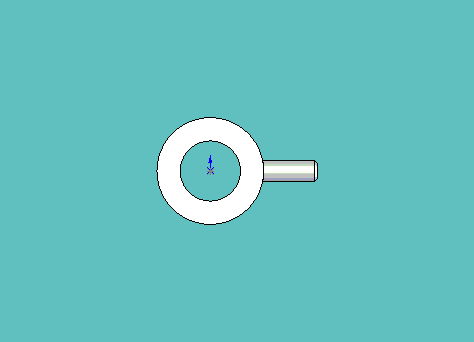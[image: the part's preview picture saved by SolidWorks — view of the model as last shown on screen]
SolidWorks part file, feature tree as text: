
SOLIDWORKS PART (.sldprt)
format: sldprt  version: not decoded by parser v0  size: 206,336 bytes
history: native  units: mm
features: sketch x2, material x1, extrude x1, revolve x1, chamfer x1 (+11 scaffold rows collapsed)
feature tree (17):
  scaffold x11  (default folders/planes/origin — collapsed)
  material  "Material <not specified>"
  sketch  "Sketch1"  dims[D1=12.7mm D2=7.1628mm D3=8.6614mm]
  extrude  "Extrude1"  Depth=3.175mm
  sketch  "Sketch4"  dims[c1.D1=13.081mm c1.D2=4.7752mm c1.D3=1.1938mm c2.D1=6.35mm]
  revolve  "Revolve1"  Angle=360deg
  chamfer  "Chamfer1"  Distance=0.254mm Angle=45deg
decode coverage: 5 of 5 modeling features carry decoded parameters
note: suppression state not decoded; provenance and decode notes live in map.json
